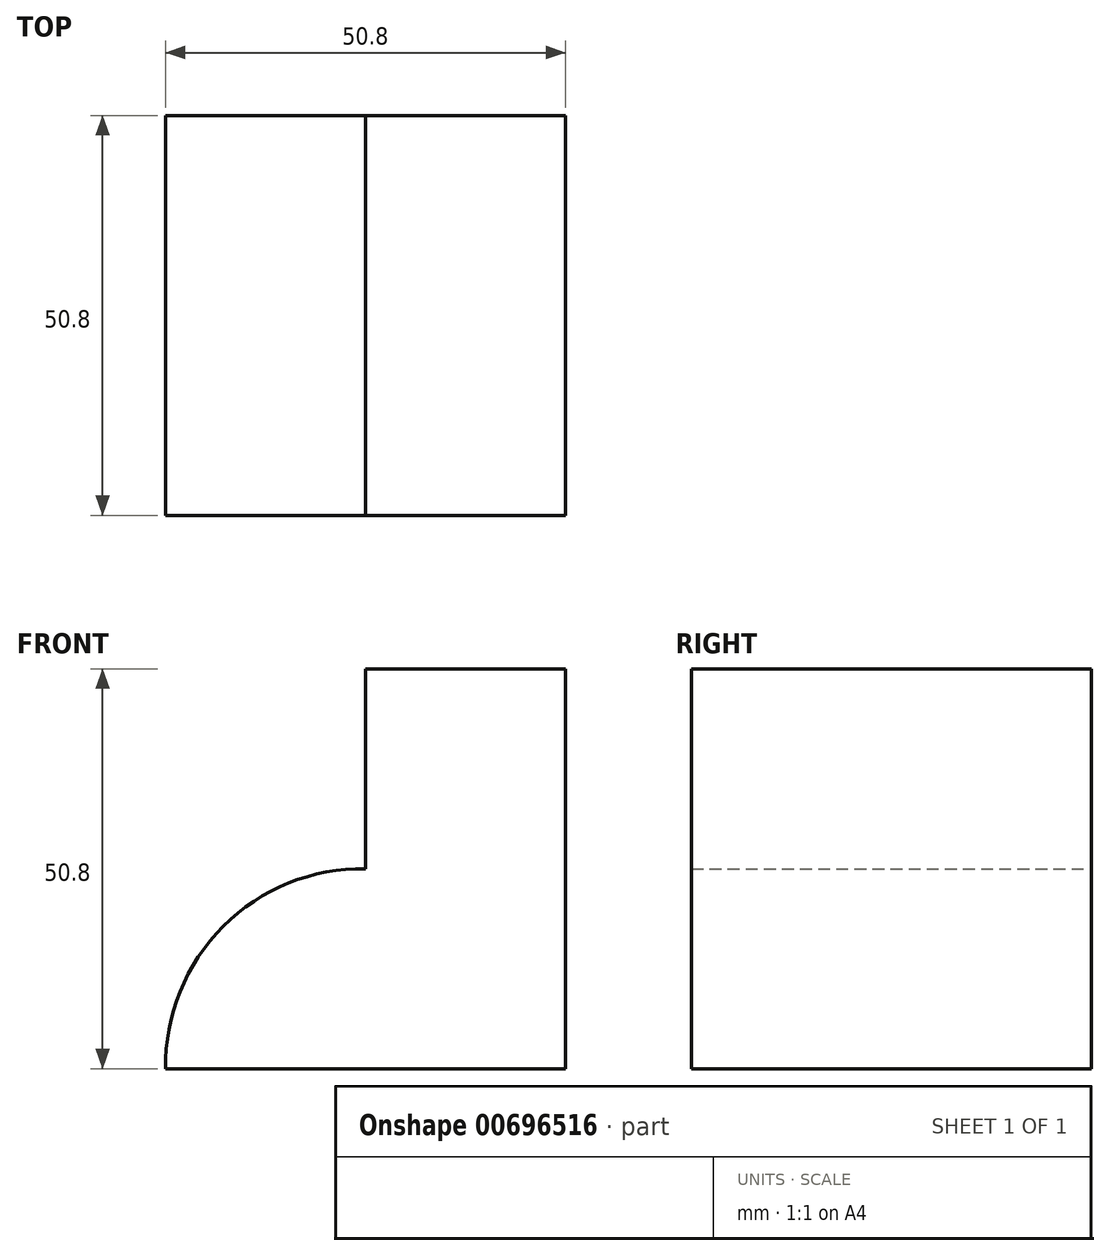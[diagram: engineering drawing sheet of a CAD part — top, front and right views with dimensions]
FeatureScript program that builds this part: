
annotation { "Feature Type Name" : "Feature", "Feature Type Description" : "" }
export const myFeature = defineFeature(function(context is Context, id is Id, definition is map)
    precondition{}
    {
        {
            var Q0;
            Q0=qCreatedBy(makeId("Front.planeOp"),FACE);
            var sketch = newSketch(context, id + "F0", { "sketchPlane" : qUnion([Q0])});
            skLineSegment(sketch, "E0", {"start": v(0, 0) * mm, "end": v(25.4, 0) * mm});
            skLineSegment(sketch, "E1", {"start": v(25.4, 0) * mm, "end": v(25.4, -50.8) * mm});
            skLineSegment(sketch, "E2", {"start": v(25.4, -50.8) * mm, "end": v(-25.4, -50.8) * mm});
            skLineSegment(sketch, "E3", {"start": v(0, 0) * mm, "end": v(0, -25.4) * mm});
            skArc(sketch, "E4", {"start": v(0, -25.4) * mm, "mid": v(-18.07, -32.73) * mm, "end": v(-25.4, -50.8) * mm});
            skSolve(sketch);
        }
        {
            var Q0;
            Q0 = qSketchRegion(id + "F0", true);
            extrude(context, id + "F1", {"entities" : qUnion([Q0]), "depth" : 50.8 * mm, "offsetDistance" : 25.4 * mm});
        }
    });
